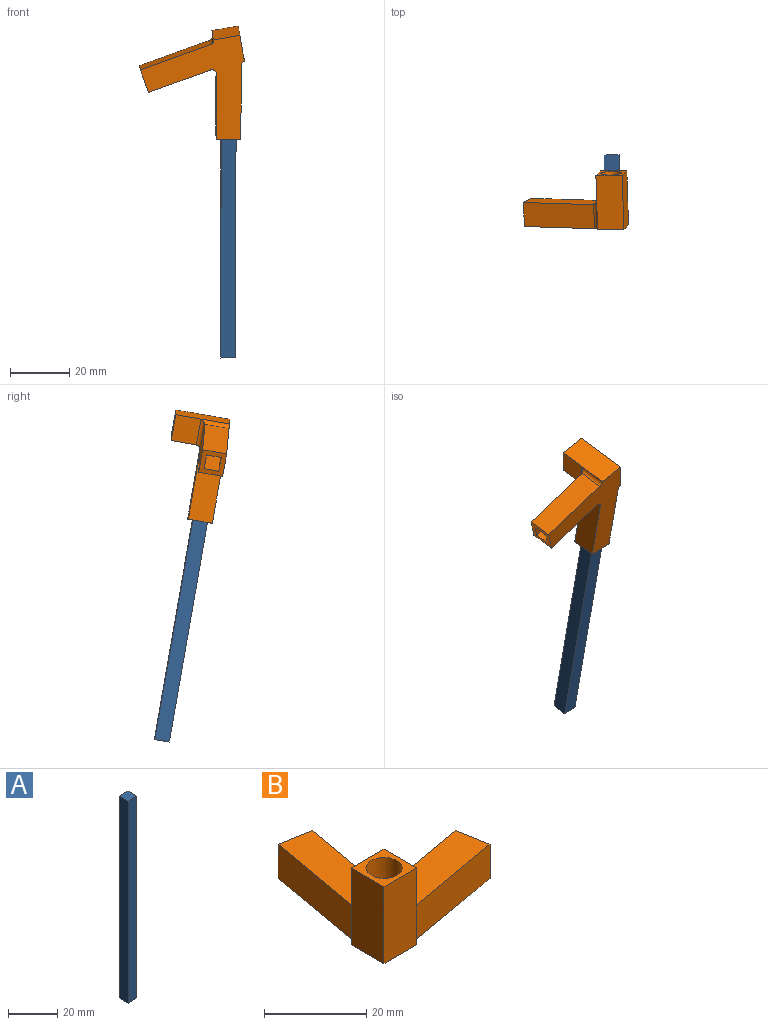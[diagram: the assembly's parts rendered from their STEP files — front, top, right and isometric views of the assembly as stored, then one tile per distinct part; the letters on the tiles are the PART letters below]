
ASSEMBLY  parts=2 mates=1
PART A: 6 faces, bbox 5x5x100 mm
  f0: plane 100x5mm, normal (0,1,0), area 500mm2, adj f1,f3,f4,f5
  f1: plane 100x5mm, normal (-1,0,0), area 500mm2, adj f0,f2,f4,f5
  f2: plane 100x5mm, normal (0,-1,0), area 500mm2, adj f1,f3,f4,f5
  f3: plane 100x5mm, normal (1,0,0), area 500mm2, adj f0,f2,f4,f5
  f4: plane 5x5mm, normal (0,0,1), area 25mm2, adj f0,f1,f2,f3
  f5: plane 5x5mm, normal (0,0,-1), area 25mm2, adj f0,f1,f2,f3
PART B: 31 faces, bbox 35x35x18.4 mm
  f0: plane 24.43x12.38mm, normal (0,0,1), area 197.6mm2, adj f3,f4,f12,f27,f28
  f1: plane 25.49x9.27mm, normal (0,0,1), area 125mm2, adj f10,f14,f15,f16
  f2: plane 25.49x9.27mm, normal (0,0,1), area 125mm2, adj f3,f17,f18,f19
  f3: plane 8.2x8.08mm, normal (0.17,0.98,0), area 42.2mm2, adj f0,f2,f4,f12,f13,f17,f19,f22
  f4: plane 24.72x8.23mm, normal (-0.98,0.17,0), area 205.8mm2, adj f0,f3,f13,f26,f27
  f5: plane 9x8.6mm, normal (0,1,0), area 77.4mm2, adj f6,f8,f23,f27
  f6: plane 18.4x9mm, normal (-1,0,0), area 165.6mm2, adj f5,f7,f13,f23,f26
  f7: plane 18.4x9mm, normal (0,-1,0), area 165.6mm2, adj f6,f8,f13,f23,f29
  f8: plane 9x8.6mm, normal (1,0,0), area 77.4mm2, adj f5,f7,f23,f30
  f9: plane 24.72x8.23mm, normal (0.17,-0.98,0), area 205.8mm2, adj f10,f13,f21,f29,f30
  f10: plane 8.2x8.08mm, normal (0.98,0.17,0), area 42.2mm2, adj f1,f9,f11,f13,f14,f16,f20,f21
  f11: plane 21.8x8.2mm, normal (-0.17,0.98,0), area 181.5mm2, adj f10,f13,f21,f28
  f12: plane 21.8x8.2mm, normal (0.98,-0.17,0), area 181.5mm2, adj f0,f3,f13,f28
  f13: plane 35.03x35.03mm, normal (0,0,-1), area 504.2mm2, adj f3,f4,f6,f7,f9,f10,f11,f12
  f14: plane 24.62x5mm, normal (-0.17,0.98,0), area 125mm2, adj f1,f10,f15,f20
  f15: plane 5x4.92mm, normal (0.98,0.17,0), area 25mm2, adj f1,f14,f16,f20
  f16: plane 24.62x5mm, normal (0.17,-0.98,0), area 125mm2, adj f1,f10,f15,f20
  f17: plane 24.62x5mm, normal (-0.98,0.17,0), area 125mm2, adj f2,f3,f18,f22
  f18: plane 5x4.92mm, normal (0.17,0.98,0), area 25mm2, adj f2,f17,f19,f22
  f19: plane 24.62x5mm, normal (0.98,-0.17,0), area 125mm2, adj f2,f3,f18,f22
  f20: plane 25.49x9.27mm, normal (0,0,-1), area 125mm2, adj f10,f14,f15,f16
  f21: plane 24.43x12.38mm, normal (0,0,1), area 197.6mm2, adj f9,f10,f11,f28,f30
  f22: plane 25.49x9.27mm, normal (0,0,-1), area 125mm2, adj f3,f17,f18,f19
  f23: plane 9x9mm, normal (0,0,1), area 41.7mm2, adj f5,f6,f7,f8,f25
  f24: plane 7.07x7.07mm, normal (0,0,1), area 39.3mm2, adj f25
  f25: cylinder r=3.54mm len=16.8mm, axis (0,0,-1), area 373.2mm2, adj f23,f24
  f26: cylinder r=1.6mm len=9.8mm, axis (0,0,-1), area 17.7mm2, adj f4,f6,f13,f27
  f27: cylinder r=1.6mm len=10.4mm, axis (1,0,0), area 21.9mm2, adj f0,f4,f5,f26,f28,f30
  f28: cylinder r=1.6mm len=8.21mm, axis (0,0,-1), area 25.2mm2, adj f0,f11,f12,f13,f21,f27,f30
  f29: cylinder r=1.6mm len=9.8mm, axis (0,0,1), area 17.7mm2, adj f7,f9,f13,f30
  f30: cylinder r=1.6mm len=10.4mm, axis (0,-1,0), area 21.9mm2, adj f8,f9,f21,f27,f28,f29
PLACE A rot(axis=(0.98,0,0.17),10deg) t=(62.4,29.11,-33.67)mm
PLACE B rot(axis=(-0.61,0.5,0.61),109.2deg) t=(30.92,25.87,72.7)mm
MATE fastened B.f15 <-> A.f4  axis (0,0.17,-0.99) through (28.21,33.2,68.63)mm
